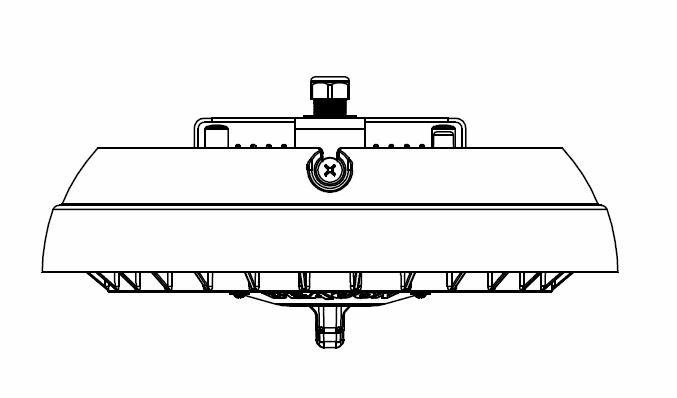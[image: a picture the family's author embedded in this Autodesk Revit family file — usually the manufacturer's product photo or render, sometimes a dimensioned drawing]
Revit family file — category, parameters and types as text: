
# Revit family: MET30
name_source: partatom
category: Lighting Fixtures
revit_build: Autodesk Revit Architecture 2012 (Build: 20110309_2315(x64)
units: mm (PartAtom-declared; Revit-internal decimal feet)

## types (12) — shared parameters
Apparent Load = 0 VA
Color Filter = 16777215
Default Elevation = 48"
Description = 30” Metropolis Luminaire
Dimming Lamp Color Temperature Shift = <None>
Lamp = LED
Light Bulb Material = Hubbell - Glass
Manufacturer = Beacon Lighting
Manufacturer Fax = 941-751-5535
Model = Metropolis
Photometric Web File = generic
Product Documentation Link = http://www.beaconproducts.com
Product Page URL = http://www.beaconproducts.com
Tilt Angle = -90.00°
URL = http://www.beaconproducts.com
Voltage = 120 V
Wattage Comments = 55-136 W
Watts = 136 W

## per-type parameters (varying)
| type | Finish |
| Basic Black Textured | Paint - Hubbell - Basic Black Textured |
| Black Matte Textured | Paint - Hubbell - Black Matte Textured |
| Bronze Textured | Paint - Hubbell - Bronze Textured |
| Dark Bronze Textured | Paint - Hubbell - Dark Bronze Textured |
| Dark Platinum Smooth | Paint - Hubbell - Dark Platinum Smooth |
| Gray Smooth | Paint - Hubbell - Gray Smooth |
| Green Textured | Paint - Hubbell - Green Textured |
| Metallic Bronze Textured | Paint - Hubbell - Metallic Bronze Textured |
| Metallic Silver Textured | Paint - Hubbell - Metallic Silver Textured |
| Metallic Titanium Textured | Paint - Hubbell - Metallic Titanium Textured |
| Old World Iron | Paint - Hubbell - Old World Iron |
| White Texture | Paint - Hubbell - White Texture |

## geometry (parser evidence)
native form markers: Sweep x3
no freeform markers — native parametric forms only
